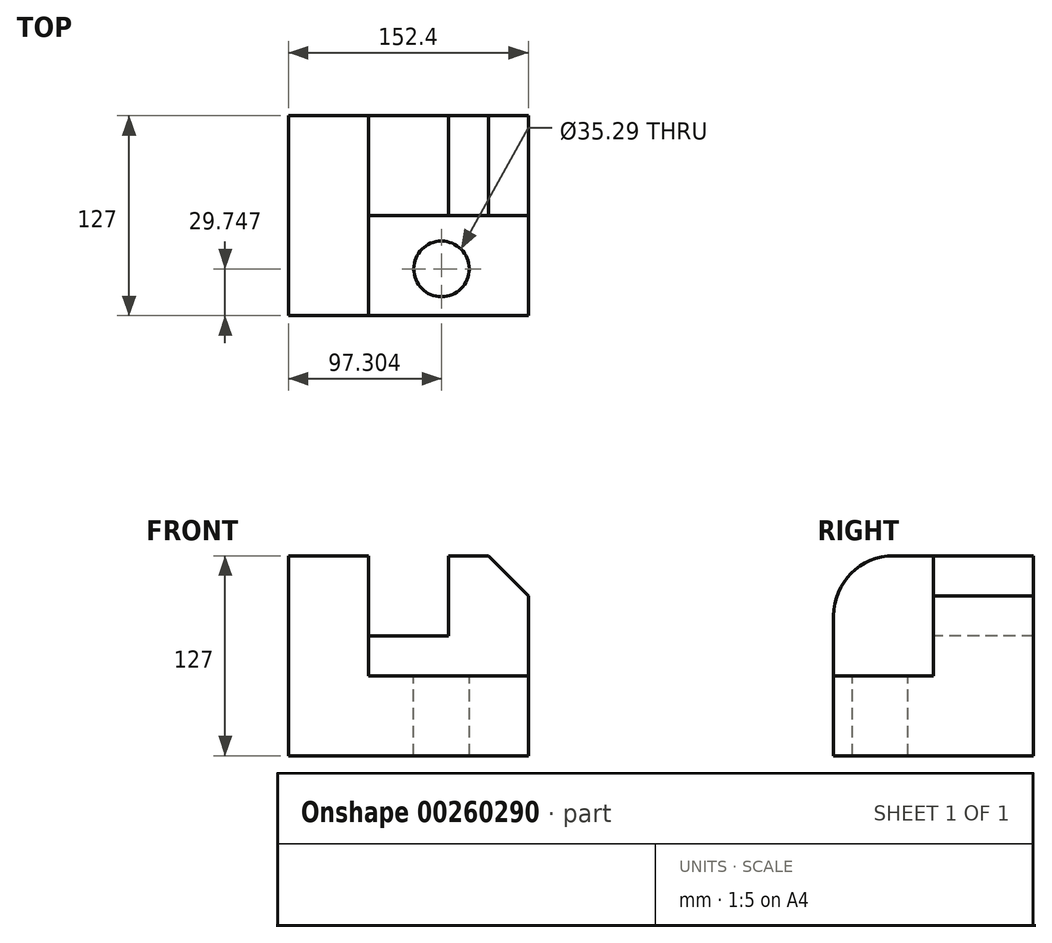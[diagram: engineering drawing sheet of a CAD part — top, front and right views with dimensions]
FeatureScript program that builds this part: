
annotation { "Feature Type Name" : "Feature", "Feature Type Description" : "" }
export const myFeature = defineFeature(function(context is Context, id is Id, definition is map)
    precondition{}
    {
        {
            var Q0;
            Q0=qCreatedBy(makeId("Front.planeOp"),FACE);
            var sketch = newSketch(context, id + "F0", { "sketchPlane" : qUnion([Q0])});
            skLineSegment(sketch, "E0.bottom", {"start": v(-66.87, 79.21) * mm, "end": v(85.53, 79.21) * mm});
            skLineSegment(sketch, "E0.top", {"start": v(-66.87, -47.79) * mm, "end": v(85.53, -47.79) * mm});
            skLineSegment(sketch, "E0.left", {"start": v(-66.87, 79.21) * mm, "end": v(-66.87, -47.79) * mm});
            skLineSegment(sketch, "E0.right", {"start": v(85.53, 79.21) * mm, "end": v(85.53, -47.79) * mm});
            skSolve(sketch);
        }
        {
            var Q0;
            Q0 = qSketchRegion(id + "F0", true);
            extrude(context, id + "F1", {"entities" : qUnion([Q0]), "depth" : 127 * mm});
        }
        {
            var Q0;
            Q0=makeQuery(id+"F1.opExtrude","CAP_FACE",FACE,{"disambiguationData":[OSD([sQuery(id+"F0.wireOp",EDGE,"E0.bottom"),sQuery(id+"F0.wireOp",EDGE,"E0.top"),sQuery(id+"F0.wireOp",EDGE,"E0.left"),sQuery(id+"F0.wireOp",EDGE,"E0.right")])],"isStart":false});
            var sketch = newSketch(context, id + "F2", { "sketchPlane" : qUnion([Q0])});
            skLineSegment(sketch, "E1.bottom", {"start": v(-16.07, 79.21) * mm, "end": v(85.53, 79.21) * mm});
            skLineSegment(sketch, "E1.top", {"start": v(-16.07, 3.01) * mm, "end": v(85.53, 3.01) * mm});
            skLineSegment(sketch, "E1.left", {"start": v(-16.07, 79.21) * mm, "end": v(-16.07, 3.01) * mm});
            skLineSegment(sketch, "E1.right", {"start": v(85.53, 79.21) * mm, "end": v(85.53, 3.01) * mm});
            skSolve(sketch);
        }
        {
            var Q0;
            Q0=makeQuery(id+"F2.imprint","IMPRINT",FACE,{"disambiguationData":[TD([[makeQuery(id+"F2.imprint","IMPRINT",EDGE,{"derivedFrom":sQuery(id+"F2.wireOp",EDGE,"E1.bottom")}),-1.0]])]});
            extrude(context, id + "F3", {"entities" : qUnion([Q0]), "operationType" : NewBodyOperationType.REMOVE, "oppositeDirection" : true, "depth" : 88.9 * mm});
        }
        {
            var Q0;
            Q0=makeQuery(id+"F1.opExtrude","CAP_EDGE",EDGE,{"disambiguationData":[OSD([sQuery(id+"F0.wireOp",EDGE,"E0.bottom")])],"isStart":false});
            fillet(context, id + "F4", {"entities" : qUnion([Q0]), "radius" : 38.1 * mm, "tangentPropagation" : true, "allowEdgeOverflow" : false});
        }
        {
            var Q0;
            Q0=makeQuery(id+"F3.boolean.opBoolean","COPY",FACE,{"derivedFrom":makeQuery(id+"F3.opExtrude","CAP_FACE",FACE,{"disambiguationData":[OSD([sQuery(id+"F2.wireOp",EDGE,"E1.bottom"),sQuery(id+"F2.wireOp",EDGE,"E1.top"),sQuery(id+"F2.wireOp",EDGE,"E1.left"),sQuery(id+"F2.wireOp",EDGE,"E1.right")])],"isStart":false})});
            extrude(context, id + "F5", {"entities" : qUnion([Q0]), "operationType" : NewBodyOperationType.ADD, "depth" : 25.4 * mm});
        }
        {
            var Q0;
            Q0=makeQuery(id+"F5.opExtrude","CAP_FACE",FACE,{"disambiguationData":[OSD([sQuery(id+"F2.wireOp",EDGE,"E1.bottom"),sQuery(id+"F2.wireOp",EDGE,"E1.top"),sQuery(id+"F2.wireOp",EDGE,"E1.left"),sQuery(id+"F2.wireOp",EDGE,"E1.right")])],"isStart":false});
            var sketch = newSketch(context, id + "F6", { "sketchPlane" : qUnion([Q0])});
            skLineSegment(sketch, "E2.bottom", {"start": v(34.73, 79.21) * mm, "end": v(-16.07, 79.21) * mm});
            skLineSegment(sketch, "E2.top", {"start": v(34.73, 28.41) * mm, "end": v(-16.07, 28.41) * mm});
            skLineSegment(sketch, "E2.left", {"start": v(34.73, 79.21) * mm, "end": v(34.73, 28.41) * mm});
            skLineSegment(sketch, "E2.right", {"start": v(-16.07, 79.21) * mm, "end": v(-16.07, 28.41) * mm});
            skSolve(sketch);
        }
        {
            var Q0;
            Q0=makeQuery(id+"F6.imprint","IMPRINT",FACE,{"disambiguationData":[TD([[makeQuery(id+"F6.imprint","IMPRINT",EDGE,{"derivedFrom":sQuery(id+"F6.wireOp",EDGE,"E2.bottom")}),-1.0]])]});
            extrude(context, id + "F7", {"entities" : qUnion([Q0]), "operationType" : NewBodyOperationType.REMOVE, "endBound" : BoundingType.THROUGH_ALL, "oppositeDirection" : true, "depth" : 25.4 * mm});
        }
        {
            var Q0;
            Q0=makeQuery(id+"F5.boolean.opBoolean","MERGE",EDGE,{"derivedFrom":[makeQuery(id+"F1.opExtrude","SWEPT_EDGE",EDGE,{"disambiguationData":[OSD([sQuery(id+"F0.wireOp",EDGE,"E0.bottom"),sQuery(id+"F0.wireOp",EDGE,"E0.right")])]}),makeQuery(id+"F5.opExtrude","SWEPT_EDGE",EDGE,{"disambiguationData":[OSD([sQuery(id+"F2.wireOp",EDGE,"E1.bottom"),sQuery(id+"F2.wireOp",EDGE,"E1.right")])]})]});
            chamfer(context, id + "F8", {"entities" : qUnion([Q0]), "width" : 25.4 * mm, "tangentPropagation" : true});
        }
        {
            var Q0;
            Q0=makeQuery(id+"F3.boolean.opBoolean","COPY",FACE,{"derivedFrom":makeQuery(id+"F3.opExtrude","SWEPT_FACE",FACE,{"disambiguationData":[OSD([sQuery(id+"F2.wireOp",EDGE,"E1.top")])]})});
            var sketch = newSketch(context, id + "F9", { "sketchPlane" : qUnion([Q0])});
            skCircle(sketch, "E3", {"center": v(30.43, -97.25) * mm, "radius": 17.65 * mm});
            skSolve(sketch);
        }
        {
            var Q0;
            Q0 = qSketchRegion(id + "F9", true);
            extrude(context, id + "F10", {"entities" : qUnion([Q0]), "operationType" : NewBodyOperationType.REMOVE, "endBound" : BoundingType.THROUGH_ALL, "oppositeDirection" : true, "depth" : 25.4 * mm});
        }
    });
